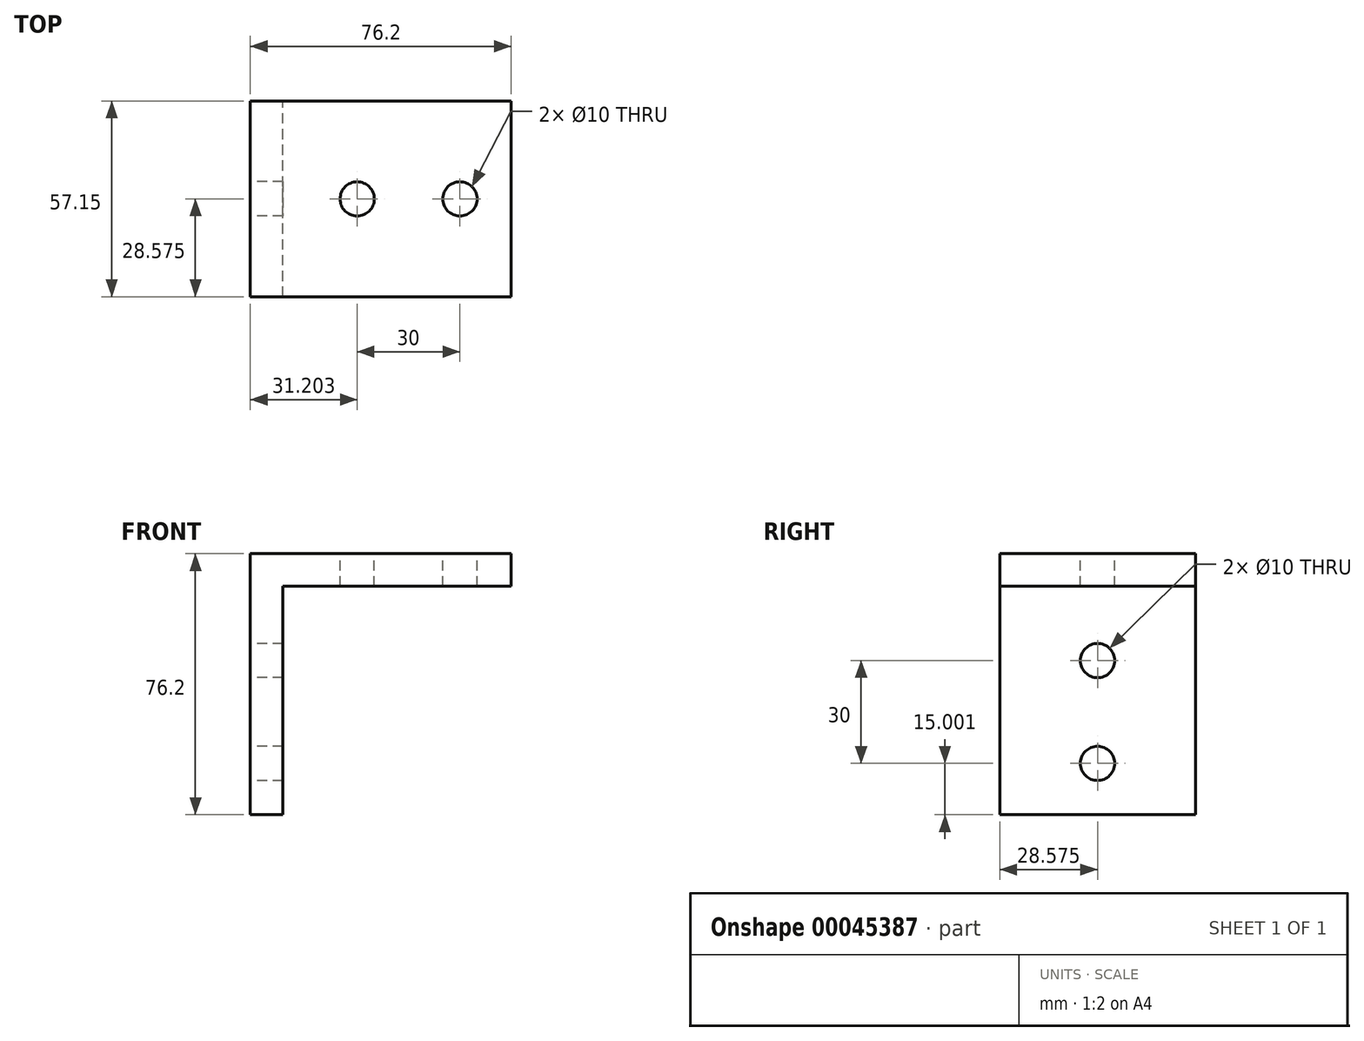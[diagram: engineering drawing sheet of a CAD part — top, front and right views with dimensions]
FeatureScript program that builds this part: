
annotation { "Feature Type Name" : "Feature", "Feature Type Description" : "" }
export const myFeature = defineFeature(function(context is Context, id is Id, definition is map)
    precondition{}
    {
        {
            var Q0;
            Q0=qCreatedBy(makeId("Front.planeOp"),FACE);
            var sketch = newSketch(context, id + "F0", { "sketchPlane" : qUnion([Q0])});
            skLineSegment(sketch, "E0.bottom", {"start": v(-39.19, 41.03) * mm, "end": v(37.01, 41.03) * mm});
            skLineSegment(sketch, "E0.top", {"start": v(-39.19, -35.17) * mm, "end": v(-29.66, -35.17) * mm});
            skLineSegment(sketch, "E0.left", {"start": v(-39.19, 41.03) * mm, "end": v(-39.19, -35.17) * mm});
            skLineSegment(sketch, "E0.right", {"start": v(37.01, 41.03) * mm, "end": v(37.01, 31.5) * mm});
            skLineSegment(sketch, "E1.top", {"start": v(37.01, 31.5) * mm, "end": v(-29.66, 31.5) * mm});
            skLineSegment(sketch, "E1.right", {"start": v(-29.66, -35.17) * mm, "end": v(-29.66, 31.5) * mm});
            skSolve(sketch);
        }
        {
            var Q0;
            Q0=makeQuery(id+"F0.imprint","IMPRINT",FACE,{"disambiguationData":[TD([[makeQuery(id+"F0.imprint","IMPRINT",EDGE,{"derivedFrom":sQuery(id+"F0.wireOp",EDGE,"E0.bottom")}),-1.0]])]});
            extrude(context, id + "F1", {"entities" : qUnion([Q0]), "depth" : 57.15 * mm});
        }
        {
            var Q0;
            Q0=makeQuery(id+"F1.opExtrude","SWEPT_FACE",FACE,{"disambiguationData":[OSD([sQuery(id+"F0.wireOp",EDGE,"E0.bottom")])]});
            var sketch = newSketch(context, id + "F2", { "sketchPlane" : qUnion([Q0])});
            skCircle(sketch, "E2", {"center": v(22.01, -28.57) * mm, "radius": 5 * mm});
            skCircle(sketch, "E3", {"center": v(-7.99, -28.58) * mm, "radius": 5 * mm});
            skSolve(sketch);
        }
        {
            var Q0;
            Q0=makeQuery(id+"F1.opExtrude","SWEPT_FACE",FACE,{"disambiguationData":[OSD([sQuery(id+"F0.wireOp",EDGE,"E0.left")])]});
            var sketch = newSketch(context, id + "F3", { "sketchPlane" : qUnion([Q0])});
            skCircle(sketch, "E4", {"center": v(28.57, -20.17) * mm, "radius": 5 * mm});
            skCircle(sketch, "E5", {"center": v(28.58, 9.83) * mm, "radius": 5 * mm});
            skSolve(sketch);
        }
        {
            var Q0;
            Q0=makeQuery(id+"F3.imprint","IMPRINT",FACE,{"disambiguationData":[TD([[makeQuery(id+"F3.imprint","IMPRINT",EDGE,{"derivedFrom":sQuery(id+"F3.wireOp",EDGE,"E4")}),1.0]])]});
            var Q1;
            Q1=makeQuery(id+"F3.imprint","IMPRINT",FACE,{"disambiguationData":[TD([[makeQuery(id+"F3.imprint","IMPRINT",EDGE,{"derivedFrom":sQuery(id+"F3.wireOp",EDGE,"E5")}),1.0]])]});
            extrude(context, id + "F4", {"entities" : qUnion([Q0, Q1]), "operationType" : NewBodyOperationType.REMOVE, "oppositeDirection" : true, "depth" : 25 * mm});
        }
        {
            var Q0;
            Q0=makeQuery(id+"F2.imprint","IMPRINT",FACE,{"disambiguationData":[TD([[makeQuery(id+"F2.imprint","IMPRINT",EDGE,{"derivedFrom":sQuery(id+"F2.wireOp",EDGE,"E3")}),1.0]])]});
            var Q1;
            Q1=makeQuery(id+"F2.imprint","IMPRINT",FACE,{"disambiguationData":[TD([[makeQuery(id+"F2.imprint","IMPRINT",EDGE,{"derivedFrom":sQuery(id+"F2.wireOp",EDGE,"E2")}),1.0]])]});
            extrude(context, id + "F5", {"entities" : qUnion([Q0, Q1]), "operationType" : NewBodyOperationType.REMOVE, "oppositeDirection" : true, "depth" : 25 * mm});
        }
    });
